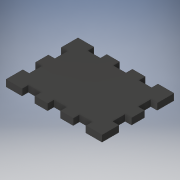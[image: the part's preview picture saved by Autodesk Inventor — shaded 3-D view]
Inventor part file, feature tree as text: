
AUTODESK INVENTOR PART (.ipt)
format: ipt  version: 2019 (Build 230136000, 136)  size: 170,496 bytes
history: native  units: mm
features: extrude x2, sketch x2, projected_geometry x1
ambient origin geometry x8: Origin, YZ Plane, XZ Plane, XY Plane, X Axis, Y Axis, Z Axis, Center Point
bodies: Solid1 (feature_tree)
feature tree (5):
  extrude  "Extrusion1"  Depth=45.0mm
  extrude  "Extrusion2"  Depth=4.0mm
  sketch  "Sketch1"  dims[d0=60.0mm d1=45.0mm]
  sketch  "Sketch2"  dims[d2=4.0mm d3=0.0mm d4=4.0mm d7=8.0mm d8=8.0mm d9=4.0mm d10=8.0mm d11=4.0mm d12=4.0mm d13=0.0mm]
  projected_geometry  "Projected Loop1"
